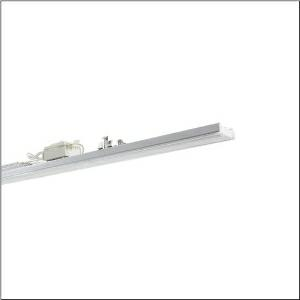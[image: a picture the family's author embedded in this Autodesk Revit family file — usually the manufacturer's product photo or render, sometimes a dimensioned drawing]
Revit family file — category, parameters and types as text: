
# Revit family: licross_r__11_recessed_mo_51tl127n485g_9b17
name_source: partatom
category: Lighting Fixtures
units: mm (PartAtom-declared; Revit-internal decimal feet)

## family parameters
Cut with Voids When Loaded = No
Host = Face
Light Source = No
Part Type = Normal
Room Calculation Point = No
Round Connector Dimension = Use Diameter
Shared = No

## types (1)
- Licross® 11 Recessed MO (1 x LED, 8950 lm, 48.5 W, 4000K)
    Apparent Load = 49 VA
    CIE Flux Codes = 67 92 99 100 100
    Color Rendering = 80
    Color Temperature = 4000K
    Default Elevation = 1800 mm
    Description = Licross® 11 Recessed MO, luminaire insert, of sheet steel, coil coated, white, length: 1.500mm, width: 66mm, height: 67mm, LED rated luminous flux: 8.950lm, light colour: 840, control gear: ON/OFF, with plug, 3-pole, with phase selection, mains connection: 220..240V, AC, 50/60Hz, rated input power: 49W, internal wiring halogen-free, primary optical cover: cover, of PMMA, light emission: direct distribution, primary light characteristic: symmetric, protection rating (complete): IP40, insulation class (complete): insulation class I (protective earthing), certification: CE, ENEC, VDE, UKCA, protection symbol: D if used in an environment without relevant dust loads with corresponding accessories, impact resistance: IK06, permissible ambient temperature for indoor applications: -35..+35°C, corresponds to IFS (International Featured Standards) requirements for safety and quality in the food industry, reducing of maximum allowable ambient temperature of 5°C with ceiling mounting, packaging unit: 1 piece
    Height = 58 mm
    Lamp = 1 x LED
    Lamp Light Flux = 8950 lm
    Lamp Power = 48.5 W
    Lamp count = 1
    Length = 1500 mm
    Luminous efficacy = 185 lm/W
    Manufacturer = Siteco
    ModVariant = No
    Model = 51TL127N485G
    Mounting Place = Ceiling
    Mounting Type = Pendant
    Number of Poles = 1
    OnlyDefault = Yes
    Power Factor = 1
    Product Name = Licross® 11 Recessed MO
    Product group = luminaire insert | ceiling pendant
    ProductGroupID = 902
    Protection Class = Protection class I
    Protection Degree = IP 40
    RLX_Detail_Level = 1
    RLX_Emergency_Light_Flux = 0 lm
    RLX_Emergency_Type = 0
    RLX_Emergency_Type_DB = No
    RlxData = <blob elided: 20765 chars, md5=9eabe1de>
    Socket = socket
    Standby Power = 0 W
    System Light Flux = 8950 lm
    System Power = 49 W
    Type Comments = Product without accessories
    Type Image = l_1296930.jpg
    URL = http://relux.com
    VarID = ---
    Voltage = 0 V
    Weight = 0.00 kg
    Width = 66 mm

## geometry (parser evidence)
native form markers: Blend x4, Sweep x10
no freeform markers — native parametric forms only
